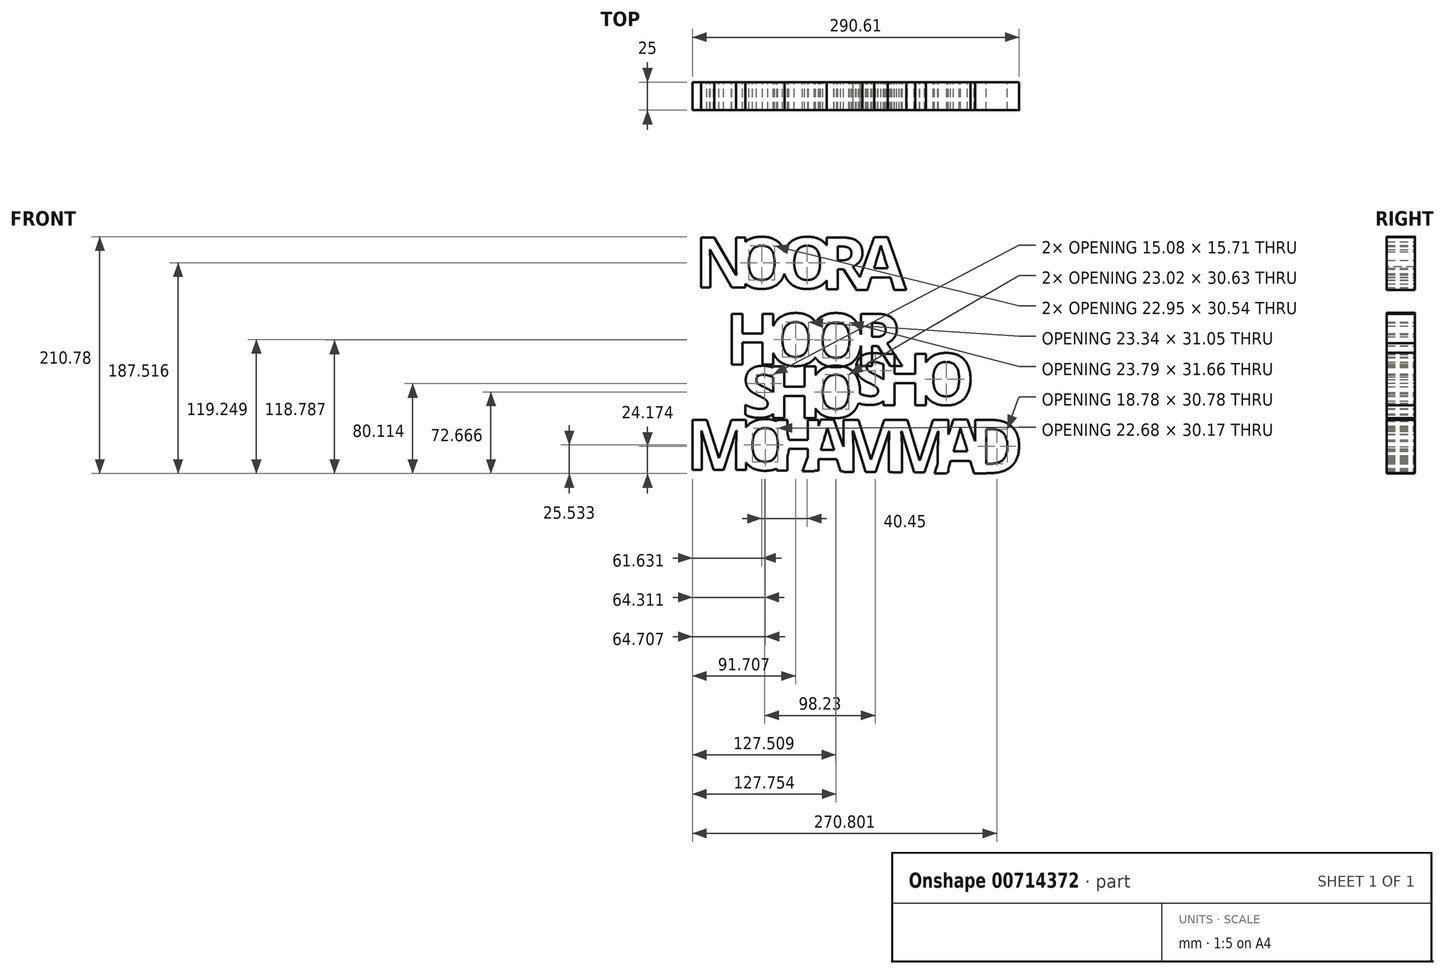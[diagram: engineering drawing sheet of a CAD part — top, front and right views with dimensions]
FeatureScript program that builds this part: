
annotation { "Feature Type Name" : "Feature", "Feature Type Description" : "" }
export const myFeature = defineFeature(function(context is Context, id is Id, definition is map)
    precondition{}
    {
        {
            var Q0;
            Q0=qCreatedBy(makeId("Front.planeOp"),FACE);
            var sketch = newSketch(context, id + "F0", { "sketchPlane" : qUnion([Q0])});
            skText(sketch, "E0", { "text": "H", "fontName": "OpenSans-Bold.ttf"});
            skText(sketch, "E1", { "text": "O", "fontName": "OpenSans-Bold.ttf"});
            skText(sketch, "E2", { "text": "O", "fontName": "OpenSans-Bold.ttf"});
            skText(sketch, "E3", { "text": "R", "fontName": "OpenSans-Bold.ttf"});
            const initialGuessF0  = {"E0": [-0.0544, -0.0332, 1, 0, 0.04545], "E1": [-0.01765, -0.03414, 1, 0, 0.0464], "E2": [0.0179, -0.03505, 1, 0, 0.0473], "E3": [0.06026, -0.03446, 1, 0, 0.04671]};
            skSetInitialGuess(sketch, initialGuessF0);
            skSolve(sketch);
        }
        {
            var Q0;
            Q0=qCreatedBy(makeId("Front.planeOp"),FACE);
            var sketch = newSketch(context, id + "F1", { "sketchPlane" : qUnion([Q0])});
            skText(sketch, "E4", { "text": "N", "fontName": "OpenSans-Bold.ttf"});
            skText(sketch, "E5", { "text": "O", "fontName": "OpenSans-Bold.ttf"});
            skText(sketch, "E6", { "text": "O", "fontName": "OpenSans-Bold.ttf"});
            skText(sketch, "E7", { "text": "R", "fontName": "OpenSans-Bold.ttf"});
            skText(sketch, "E8", { "text": "A", "fontName": "OpenSans-Bold.ttf"});
            const initialGuessF1  = {"E4": [-0.08175, 0.03514, 1, 0, 0.045], "E5": [-0.0473, 0.03451, 1, 0, 0.04563], "E6": [-0.00685, 0.03451, 1, 0, 0.04563], "E7": [0.03002, 0.03381, 1, 0, 0.04633], "E8": [0.06142, 0.03316, 1, 0, 0.04698]};
            skSetInitialGuess(sketch, initialGuessF1);
            skSolve(sketch);
        }
        {
            var Q0;
            Q0=qCreatedBy(makeId("Front.planeOp"),FACE);
            var sketch = newSketch(context, id + "F2", { "sketchPlane" : qUnion([Q0])});
            skText(sketch, "E9", { "text": "M", "fontName": "OpenSans-Bold.ttf"});
            skText(sketch, "E10", { "text": "O", "fontName": "OpenSans-Bold.ttf"});
            skText(sketch, "E11", { "text": "H", "fontName": "OpenSans-Bold.ttf"});
            skText(sketch, "E12", { "text": "A", "fontName": "OpenSans-Bold.ttf"});
            skText(sketch, "E13", { "text": "M", "fontName": "OpenSans-Bold.ttf"});
            skText(sketch, "E14", { "text": "M", "fontName": "OpenSans-Bold.ttf"});
            skText(sketch, "E15", { "text": "A", "fontName": "OpenSans-Bold.ttf"});
            skText(sketch, "E16", { "text": "D", "fontName": "OpenSans-Bold.ttf"});
            const initialGuessF2  = {"E9": [-0.08933, -0.12712, 1, 0, 0.045], "E10": [-0.04392, -0.1272, 1, 0, 0.04508], "E11": [-0.01432, -0.12772, 1, 0, 0.0456], "E12": [0.01424, -0.12824, 1, 0, 0.04612], "E13": [0.04488, -0.12876, 1, 0, 0.04664], "E14": [0.08799, -0.12928, 1, 0, 0.04716], "E15": [0.1316, -0.13031, 1, 0, 0.0482], "E16": [0.16173, -0.1298, 1, 0, 0.04767]};
            skSetInitialGuess(sketch, initialGuessF2);
            skSolve(sketch);
        }
        {
            var Q0;
            Q0=qCreatedBy(makeId("Front.planeOp"),FACE);
            var sketch = newSketch(context, id + "F3", { "sketchPlane" : qUnion([Q0])});
            skText(sketch, "E17", { "text": "S", "fontName": "OpenSans-Bold.ttf"});
            skText(sketch, "E18", { "text": "H", "fontName": "OpenSans-Bold.ttf"});
            skText(sketch, "E19", { "text": "O", "fontName": "OpenSans-Bold.ttf"});
            skText(sketch, "E20", { "text": "S", "fontName": "OpenSans-Bold.ttf"});
            skText(sketch, "E21", { "text": "H", "fontName": "OpenSans-Bold.ttf"});
            skText(sketch, "E22", { "text": "O", "fontName": "OpenSans-Bold.ttf"});
            const initialGuessF3  = {"E17": [-0.0397, -0.0801, 1, 0, 0.04545], "E18": [-0.01765, -0.08105, 1, 0, 0.0464], "E19": [0.0185, -0.08041, 1, 0, 0.04577], "E20": [0.05853, -0.06871, 1, 0, 0.04545], "E21": [0.08058, -0.06966, 1, 0, 0.0464], "E22": [0.11673, -0.06903, 1, 0, 0.04577]};
            skSetInitialGuess(sketch, initialGuessF3);
            skSolve(sketch);
        }
        {
            var Q0;
            Q0 = qSketchRegion(id + "F0", true);
            extrude(context, id + "F4", {"entities" : qUnion([Q0]), "depth" : 25 * mm, "offsetDistance" : 25 * mm});
        }
        {
            var Q0;
            Q0 = qSketchRegion(id + "F1", true);
            extrude(context, id + "F5", {"entities" : qUnion([Q0]), "depth" : 25 * mm, "offsetDistance" : 25 * mm});
        }
        {
            var Q0;
            Q0 = qSketchRegion(id + "F3", true);
            var Q1;
            Q1 = qSketchRegion(id + "F2", true);
            extrude(context, id + "F6", {"entities" : qUnion([Q0, Q1]), "depth" : 25 * mm, "offsetDistance" : 25 * mm});
        }
    });
